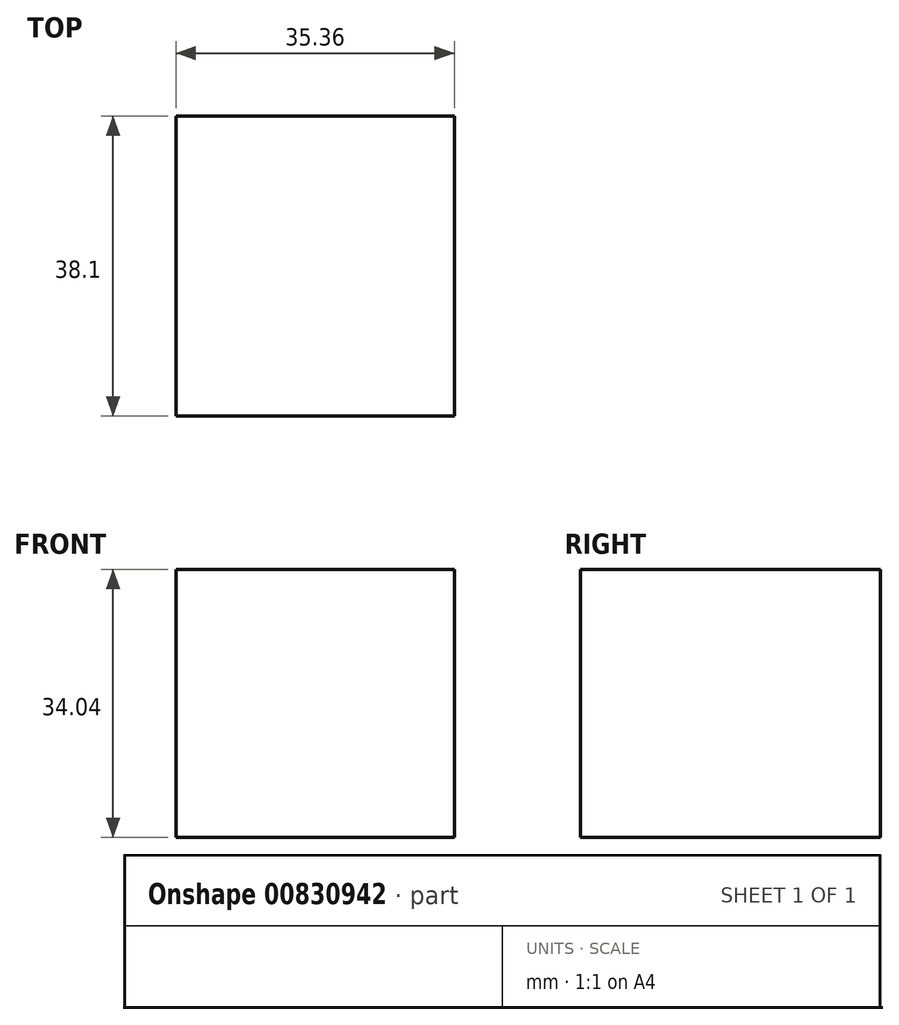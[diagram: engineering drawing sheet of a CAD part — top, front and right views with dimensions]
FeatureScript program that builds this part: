
annotation { "Feature Type Name" : "Feature", "Feature Type Description" : "" }
export const myFeature = defineFeature(function(context is Context, id is Id, definition is map)
    precondition{}
    {
        {
            var Q0;
            Q0=qCreatedBy(makeId("Front.planeOp"),FACE);
            var sketch = newSketch(context, id + "F0", { "sketchPlane" : qUnion([Q0])});
            skPoint(sketch, "E0.0", {"position": v(0, 0) * mm});
            skLineSegment(sketch, "E1.bottom", {"start": v(0, 0) * mm, "end": v(-35.36, 0) * mm});
            skLineSegment(sketch, "E1.top", {"start": v(0, 34.04) * mm, "end": v(-35.36, 34.04) * mm});
            skLineSegment(sketch, "E1.left", {"start": v(0, 0) * mm, "end": v(0, 34.04) * mm});
            skLineSegment(sketch, "E1.right", {"start": v(-35.36, 0) * mm, "end": v(-35.36, 34.04) * mm});
            skSolve(sketch);
        }
        {
            var Q0;
            Q0=makeQuery(id+"F0.imprint","IMPRINT",FACE,{"disambiguationData":[TD([[makeQuery(id+"F0.imprint","IMPRINT",EDGE,{"derivedFrom":sQuery(id+"F0.wireOp",EDGE,"E1.bottom")}),-1.0]])]});
            extrude(context, id + "F1", {"entities" : qUnion([Q0]), "depth" : 38.1 * mm, "offsetDistance" : 25.4 * mm});
        }
    });
